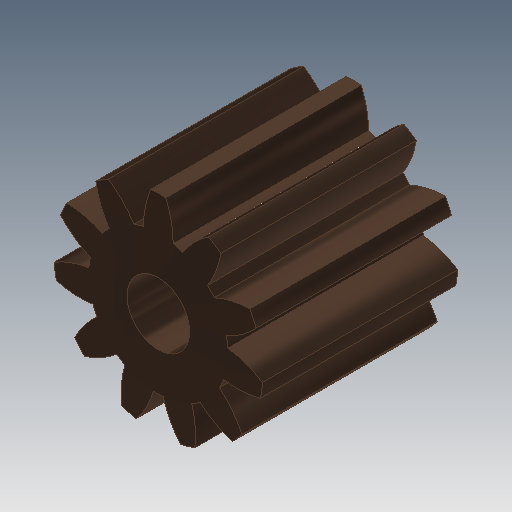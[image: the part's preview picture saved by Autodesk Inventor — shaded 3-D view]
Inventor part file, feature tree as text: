
AUTODESK INVENTOR PART (.ipt)
format: ipt  version: 2017 (Build 210142000, 142)  size: 215,040 bytes
history: native  units: mm (DEFAULTED — no unit token found)
features: plane x3, other x3, sketch x3, extrude x1, hole x1
ambient origin geometry x8: Origin, YZ Plane, XZ Plane, XY Plane, X Axis, Y Axis, Z Axis, Center Point
bodies: Solid1 (feature_tree)
feature tree (11):
  extrude  "Extrusion1"  Depth=2.5mm TaperAngle=0.0deg
  plane  "Work Plane2"
  plane  "Work Plane8"
  plane  "Work Plane9"
  other  "Цилиндрическое зубчатое зацепление"
  hole  "Отверстие1"  [1 undecoded]
  sketch  "Sketch1"  dims[d0=2.6719mm d1=2.5mm d2=0.0mm]
  sketch  "Sketch2"  dims[d3=2.237288mm d4=10.0mm d5=0.0mm d16=6.0mm d17=0.0mm d34=2.855993mm d39=0.0mm d41=0.0mm d43=6.0mm d46=6.0mm d47=0.0mm d48=0.0mm d49=0.8mm d50=6.0mm d51=4.0mm d52=2.0mm d53=90.0deg d54=8.0mm d55=20.594885mm]
  other  "Srf1"
  sketch  "Эскиз3"
  other  "Средний диаметр"
note: 1 required parameter value undecoded (feature->parameter linkage not recoverable at this tier; creation-order binding heuristic only, values carry confidence <= 0.55)
